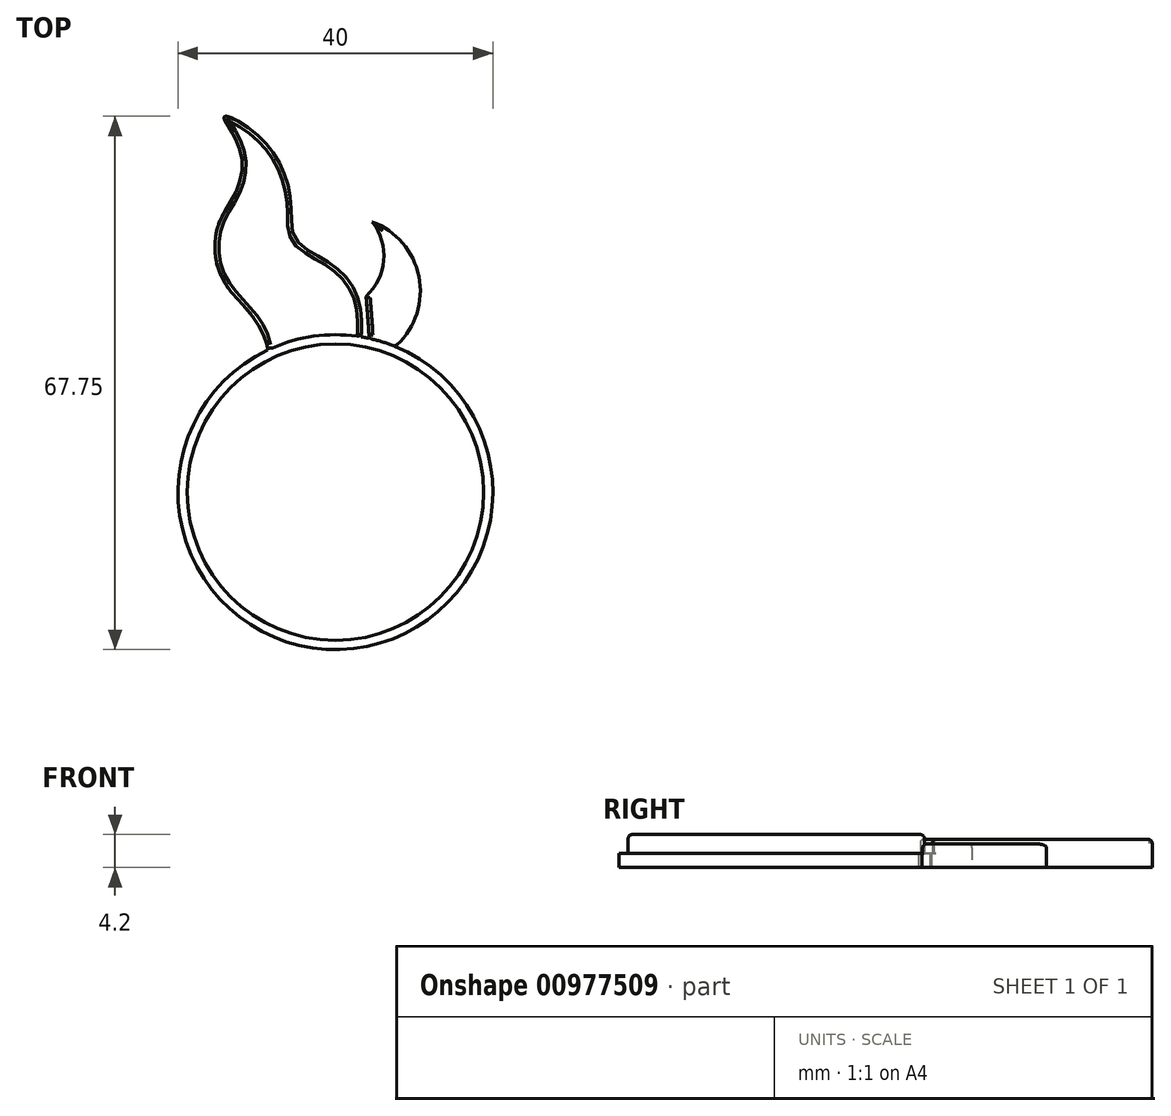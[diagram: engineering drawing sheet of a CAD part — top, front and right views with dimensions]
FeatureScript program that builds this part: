
annotation { "Feature Type Name" : "Feature", "Feature Type Description" : "" }
export const myFeature = defineFeature(function(context is Context, id is Id, definition is map)
    precondition{}
    {
        {
            var Q0;
            Q0=qCreatedBy(makeId("Top.planeOp"),FACE);
            var sketch = newSketch(context, id + "F0", { "sketchPlane" : qUnion([Q0]), "disableImprinting" : false});
            skCircle(sketch, "E0", {"center": v(0, 0) * mm, "radius": 20 * mm});
            skFitSpline(sketch, "E1", {"points": [v(3.25, 19.73) * mm, v(-4.57, 31.54) * mm, v(-5.62, 36.18) * mm, v(-8.82, 44.27) * mm, v(-14.1, 47.69) * mm, v(-12.23, 43.8) * mm, v(-12.73, 37.97) * mm, v(-15, 33.53) * mm, v(-14.07, 26.6) * mm, v(-8.6, 18.06) * mm], "startDerivative": vector(18.03, 167.88) * mm, "endDerivative": vector(14.05, -92.14) * mm});
            skArc(sketch, "E2", {"start": v(7.58, 18.5) * mm, "mid": v(10.63, 27.24) * mm, "end": v(4.68, 34.33) * mm});
            skArc(sketch, "E3", {"start": v(3.89, 24.86) * mm, "mid": v(6.13, 29.44) * mm, "end": v(4.68, 34.33) * mm});
            skFitSpline(sketch, "E4", {"points": [v(3.89, 24.86) * mm, v(4.26, 19.54) * mm], "startDerivative": vector(0.37, -4.22) * mm, "endDerivative": vector(0.17, -5.03) * mm});
            skCircle(sketch, "E5", {"center": v(0, 0) * mm, "radius": 18.82 * mm});
            skSolve(sketch);
        }
        {
            var Q0;
            Q0=makeQuery(id+"F0.imprint","IMPRINT",FACE,{"disambiguationData":[TD([[makeQuery(id+"F0.imprint","IMPRINT",EDGE,{"derivedFrom":sQuery(id+"F0.wireOp",EDGE,"E5")}),1.0]])]});
            extrude(context, id + "F1", {"entities" : qUnion([Q0]), "depth" : 4.2 * mm, "offsetDistance" : 25 * mm});
        }
        {
            var Q0;
            Q0=makeQuery(id+"F0.imprint","IMPRINT",FACE,{"disambiguationData":[TD([[makeQuery(id+"F0.imprint","IMPRINT",EDGE,{"derivedFrom":sQuery(id+"F0.wireOp",EDGE,"E5")}),-1.0]])]});
            extrude(context, id + "F2", {"entities" : qUnion([Q0]), "operationType" : NewBodyOperationType.ADD, "depth" : 1.8 * mm, "offsetDistance" : 25 * mm});
        }
        {
            var Q0;
            {var subQ0=sQuery(id+"F0.wireOp",EDGE,"E2");Q0=makeQuery(id+"F0.imprint","IMPRINT",FACE,{"disambiguationData":[TD([[makeQuery(id+"F0.imprint","IMPRINT",EDGE,{"derivedFrom":subQ0}),1.0]])]});}
            extrude(context, id + "F3", {"entities" : qUnion([Q0]), "operationType" : NewBodyOperationType.ADD, "depth" : 3 * mm, "offsetDistance" : 25 * mm});
        }
        {
            var Q0;
            {var subQ0=sQuery(id+"F0.wireOp",EDGE,"E1");Q0=makeQuery(id+"F0.imprint","IMPRINT",FACE,{"disambiguationData":[TD([[makeQuery(id+"F0.imprint","IMPRINT",EDGE,{"derivedFrom":subQ0}),1.0]])]});}
            extrude(context, id + "F4", {"entities" : qUnion([Q0]), "operationType" : NewBodyOperationType.ADD, "depth" : 3.6 * mm, "offsetDistance" : 25 * mm});
        }
        {
            var Q0;
            Q0=makeQuery(id+"F1.opExtrude","CAP_FACE",FACE,{"disambiguationData":[OSD([sQuery(id+"F0.wireOp",EDGE,"E5")])],"isStart":false});
            var Q1;
            Q1=makeQuery(id+"F3.opExtrude","CAP_FACE",FACE,{"disambiguationData":[OSD([sQuery(id+"F0.wireOp",EDGE,"E0"),sQuery(id+"F0.wireOp",EDGE,"E2"),sQuery(id+"F0.wireOp",EDGE,"E3"),sQuery(id+"F0.wireOp",EDGE,"E4")])],"isStart":false});
            var Q2;
            Q2=makeQuery(id+"F4.opExtrude","CAP_EDGE",EDGE,{"disambiguationData":[OSD([sQuery(id+"F0.wireOp",EDGE,"E0")])],"isStart":false});
            var Q3;
            {var subQ0=sQuery(id+"F0.wireOp",EDGE,"E0");var subQ1=sQuery(id+"F0.wireOp",EDGE,"E2");Q3=makeQuery(id+"F3.boolean.opBoolean","SPLIT",EDGE,{"disambiguationData":[topologyDisambiguationEdgeConnected([makeQuery(id+"F3.opExtrude","SWEPT_FACE",FACE,{"disambiguationData":[OSD([subQ0])]})])],"derivedFrom":makeQuery(id+"F3.opExtrude","SWEPT_EDGE",EDGE,{"disambiguationData":[OSD([subQ0,subQ1])]})});}
            var Q4;
            {var subQ0=sQuery(id+"F0.wireOp",EDGE,"E0");var subQ1=sQuery(id+"F0.wireOp",EDGE,"E4");Q4=makeQuery(id+"F3.boolean.opBoolean","SPLIT",EDGE,{"disambiguationData":[topologyDisambiguationEdgeConnected([makeQuery(id+"F3.opExtrude","SWEPT_FACE",FACE,{"disambiguationData":[OSD([subQ0])]})])],"derivedFrom":makeQuery(id+"F3.opExtrude","SWEPT_EDGE",EDGE,{"disambiguationData":[OSD([subQ0,subQ1])]})});}
            fillet(context, id + "F5", {"entities" : qUnion([Q0, Q1, Q2, Q3, Q4]), "radius" : 0.5 * mm, "tangentPropagation" : true, "defaultsChanged" : false, "vertexSettings" : [], "allowEdgeOverflow" : false});
        }
        {
            var Q0;
            Q0=makeQuery(id+"F4.opExtrude","CAP_FACE",FACE,{"disambiguationData":[OSD([sQuery(id+"F0.wireOp",EDGE,"E0"),sQuery(id+"F0.wireOp",EDGE,"E1")])],"isStart":false});
            fillet(context, id + "F6", {"entities" : qUnion([Q0]), "tangentPropagation" : true, "radius" : 0.5 * mm, "defaultsChanged" : true, "vertexSettings" : [], "allowEdgeOverflow" : false});
        }
    });
